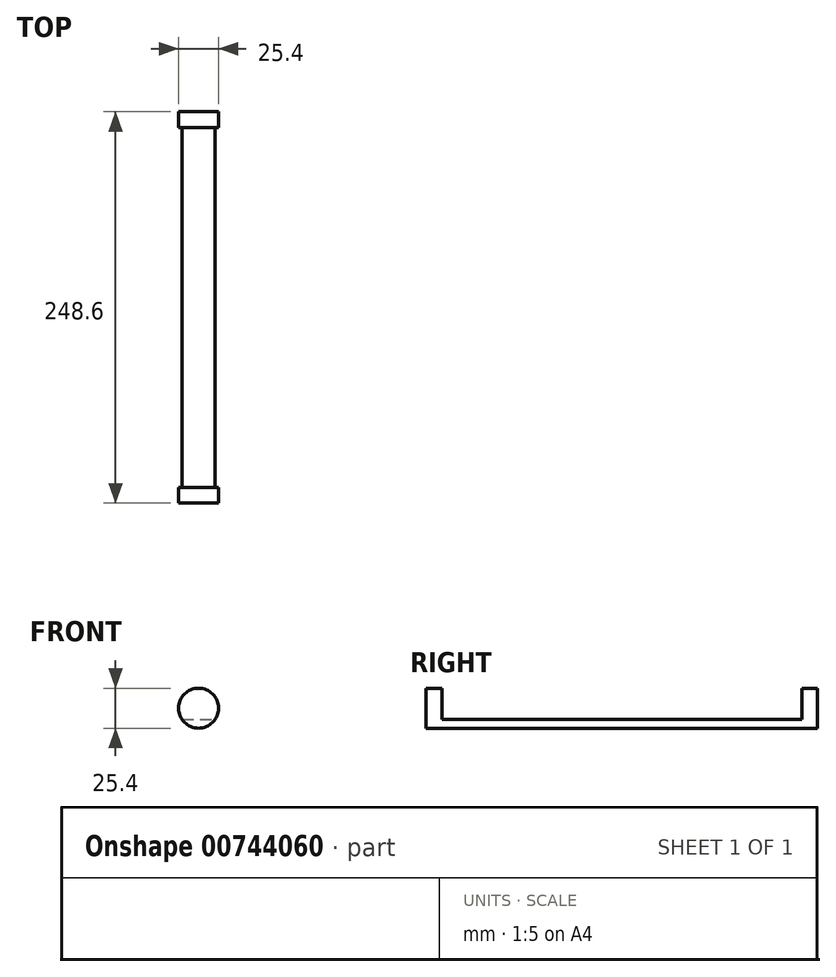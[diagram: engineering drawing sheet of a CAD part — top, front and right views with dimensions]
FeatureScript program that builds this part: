
annotation { "Feature Type Name" : "Feature", "Feature Type Description" : "" }
export const myFeature = defineFeature(function(context is Context, id is Id, definition is map)
    precondition{}
    {
        {
            var Q0;
            Q0=qCreatedBy(makeId("Front.planeOp"),FACE);
            var sketch = newSketch(context, id + "F0", { "sketchPlane" : qUnion([Q0])});
            skCircle(sketch, "E0", {"center": v(0, 0) * mm, "radius": 12.7 * mm});
            skSolve(sketch);
        }
        {
            var Q0;
            Q0 = qSketchRegion(id + "F0", true);
            extrude(context, id + "F1", {"entities" : qUnion([Q0]), "depth" : 10 * mm, "offsetDistance" : 25.4 * mm});
        }
        {
            var Q0;
            Q0=makeQuery(id+"F1.opExtrude","CAP_FACE",FACE,{"disambiguationData":[OSD([sQuery(id+"F0.wireOp",EDGE,"E0")])],"isStart":false});
            var sketch = newSketch(context, id + "F2", { "sketchPlane" : qUnion([Q0])});
            skArc(sketch, "E1", {"start": v(-10.6, -6.99) * mm, "mid": v(0, -12.7) * mm, "end": v(10.6, -6.99) * mm});
            skLineSegment(sketch, "E2", {"start": v(-10.6, -6.99) * mm, "end": v(10.6, -6.99) * mm});
            skSolve(sketch);
        }
        {
            var Q0;
            Q0 = qSketchRegion(id + "F2", true);
            extrude(context, id + "F3", {"entities" : qUnion([Q0]), "operationType" : NewBodyOperationType.ADD, "depth" : 228.6 * mm, "offsetDistance" : 25.4 * mm});
        }
        {
            var Q0;
            Q0=makeQuery(id+"F3.opExtrude","CAP_FACE",FACE,{"disambiguationData":[OSD([sQuery(id+"F2.wireOp",EDGE,"E1"),sQuery(id+"F2.wireOp",EDGE,"E2")])],"isStart":false});
            var sketch = newSketch(context, id + "F4", { "sketchPlane" : qUnion([Q0])});
            skCircle(sketch, "E3", {"center": v(0, 0) * mm, "radius": 12.7 * mm});
            skSolve(sketch);
        }
        {
            var Q0;
            Q0 = qSketchRegion(id + "F4", true);
            extrude(context, id + "F5", {"entities" : qUnion([Q0]), "operationType" : NewBodyOperationType.ADD, "depth" : 10 * mm, "offsetDistance" : 25.4 * mm});
        }
    });
